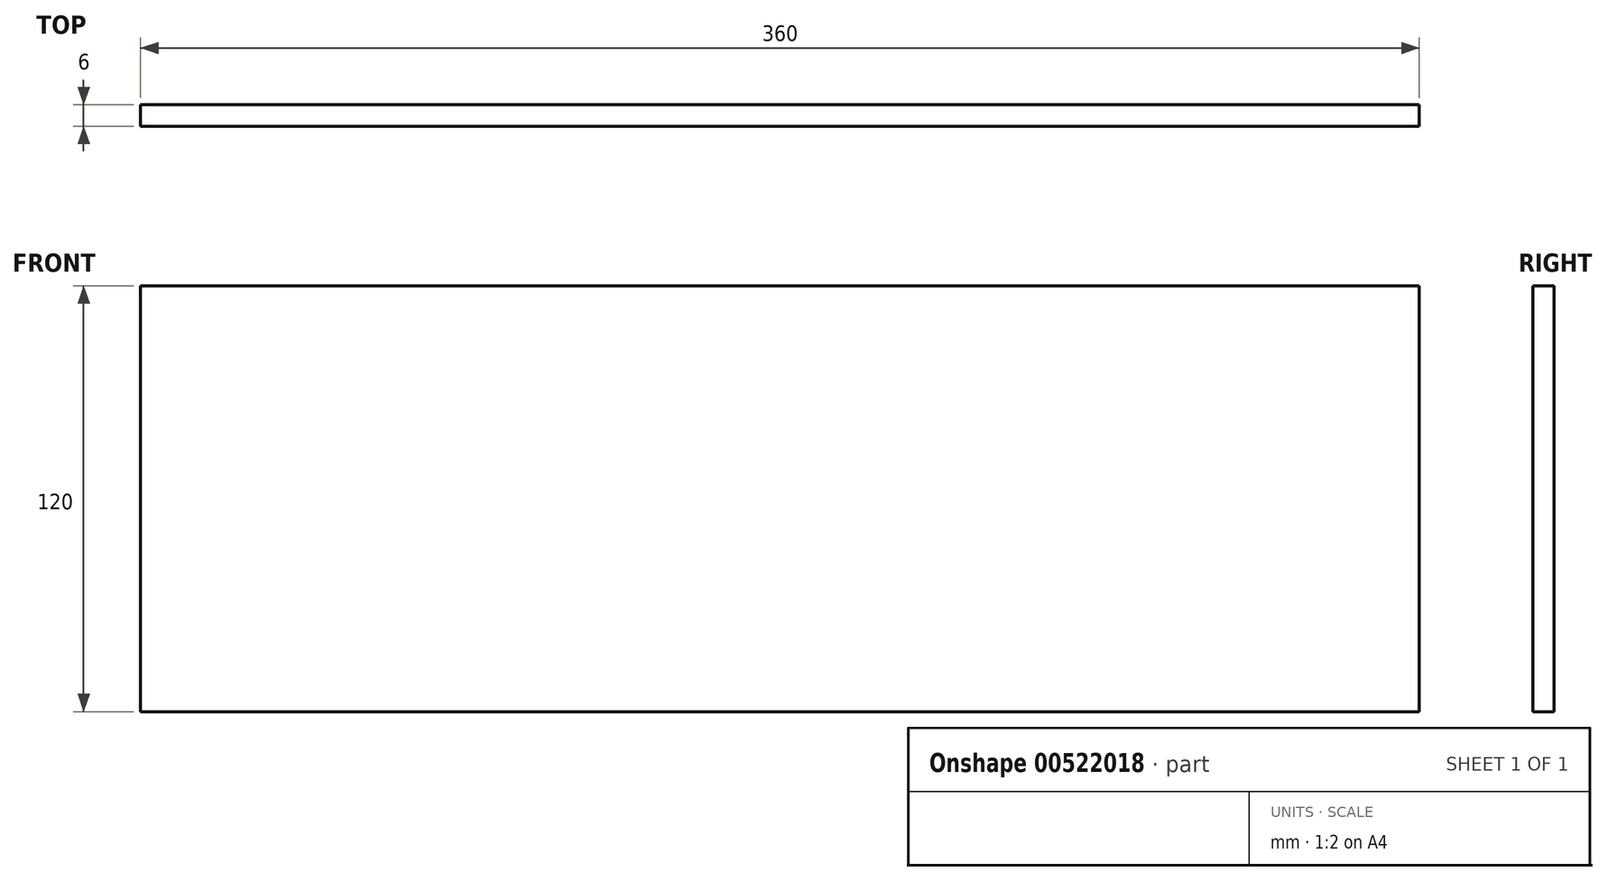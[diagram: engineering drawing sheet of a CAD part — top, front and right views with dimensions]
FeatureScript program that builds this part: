
annotation { "Feature Type Name" : "Feature", "Feature Type Description" : "" }
export const myFeature = defineFeature(function(context is Context, id is Id, definition is map)
    precondition{}
    {
        {
            var Q0;
            Q0=qCreatedBy(makeId("Front.planeOp"),FACE);
            var sketch = newSketch(context, id + "F0", { "sketchPlane" : qUnion([Q0])});
            skLineSegment(sketch, "E0.bottom", {"start": v(0, 0) * mm, "end": v(360, 0) * mm});
            skLineSegment(sketch, "E0.top", {"start": v(0, 120) * mm, "end": v(360, 120) * mm});
            skLineSegment(sketch, "E0.left", {"start": v(0, 0) * mm, "end": v(0, 120) * mm});
            skLineSegment(sketch, "E0.right", {"start": v(360, 0) * mm, "end": v(360, 120) * mm});
            skSolve(sketch);
        }
        {
            var Q0;
            Q0=makeQuery(id+"F0.imprint","IMPRINT",FACE,{"disambiguationData":[TD([[makeQuery(id+"F0.imprint","IMPRINT",EDGE,{"derivedFrom":sQuery(id+"F0.wireOp",EDGE,"E0.bottom")}),1.0]])]});
            extrude(context, id + "F1", {"entities" : qUnion([Q0]), "depth" : 6 * mm, "offsetDistance" : 25 * mm});
        }
    });
